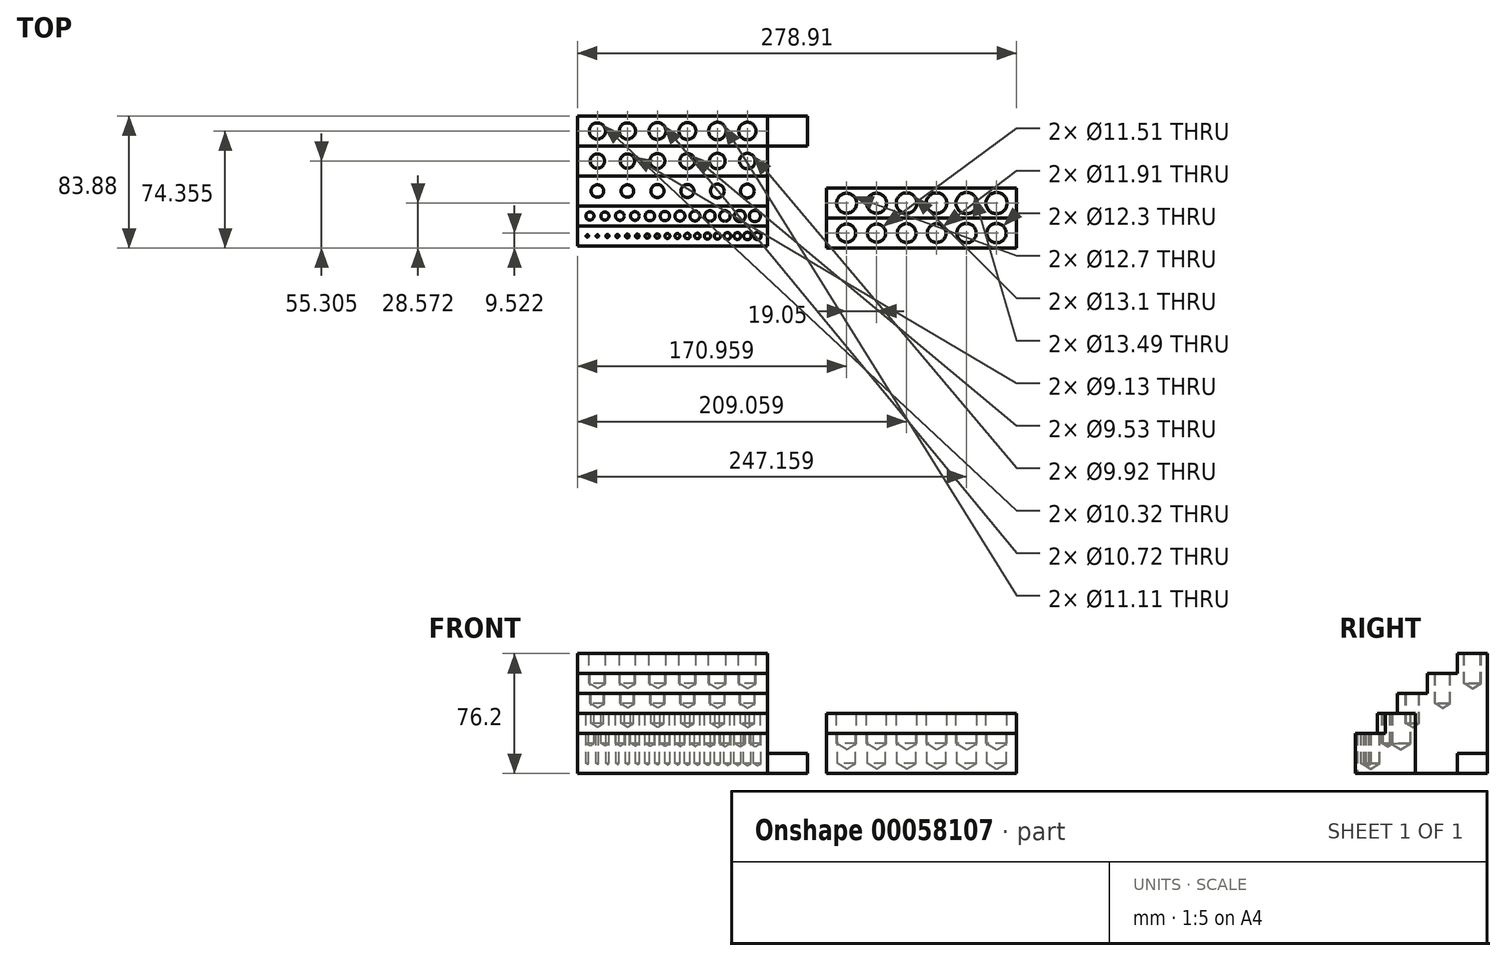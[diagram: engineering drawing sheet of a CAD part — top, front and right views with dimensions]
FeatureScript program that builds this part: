
annotation { "Feature Type Name" : "Feature", "Feature Type Description" : "" }
export const myFeature = defineFeature(function(context is Context, id is Id, definition is map)
    precondition{}
    {
        {
            var Q0;
            Q0=qCreatedBy(makeId("Top.planeOp"),FACE);
            var sketch = newSketch(context, id + "F0", { "sketchPlane" : qUnion([Q0])});
            skLineSegment(sketch, "E0.rect.bottom", {"start": v(60.32, -31.75) * mm, "end": v(-60.33, -31.75) * mm});
            skLineSegment(sketch, "E0.rect.top", {"start": v(60.33, 31.75) * mm, "end": v(-60.32, 31.75) * mm});
            skLineSegment(sketch, "E0.rect.left", {"start": v(60.32, -31.75) * mm, "end": v(60.33, 31.75) * mm});
            skLineSegment(sketch, "E0.rect.right", {"start": v(-60.33, -31.75) * mm, "end": v(-60.32, 31.75) * mm});
            skPoint(sketch, "E0.rect.middle", {"position": v(0, 0) * mm});
            skLineSegment(sketch, "E1", {"start": v(-60.33, 12.7) * mm, "end": v(60.33, 12.7) * mm});
            skLineSegment(sketch, "E2", {"start": v(-60.33, -6.35) * mm, "end": v(60.32, -6.35) * mm});
            skLineSegment(sketch, "E3", {"start": v(-60.33, -19.05) * mm, "end": v(60.33, -19.05) * mm});
            skLineSegment(sketch, "E4", {"start": v(-60.32, 31.75) * mm, "end": v(-60.32, 50.8) * mm});
            skLineSegment(sketch, "E5", {"start": v(-60.33, 50.8) * mm, "end": v(60.32, 50.8) * mm});
            skLineSegment(sketch, "E6", {"start": v(60.33, 31.75) * mm, "end": v(60.33, 50.8) * mm});
            skSolve(sketch);
        }
        {
            var Q0;
            {var subQ0=sQuery(id+"F0.wireOp",EDGE,"E0.rect.top");Q0=makeQuery(id+"F0.imprint","IMPRINT",FACE,{"disambiguationData":[TD([[makeQuery(id+"F0.imprint","IMPRINT",EDGE,{"derivedFrom":subQ0}),1.0]])]});}
            extrude(context, id + "F1", {"entities" : qUnion([Q0]), "depth" : 63.5 * mm});
        }
        {
            var Q0;
            {var subQ0=sQuery(id+"F0.wireOp",EDGE,"E1");Q0=makeQuery(id+"F0.imprint","IMPRINT",FACE,{"disambiguationData":[TD([[makeQuery(id+"F0.imprint","IMPRINT",EDGE,{"derivedFrom":subQ0}),-1.0]])]});}
            extrude(context, id + "F2", {"entities" : qUnion([Q0]), "operationType" : NewBodyOperationType.ADD, "depth" : 50.8 * mm});
        }
        {
            var Q0;
            {var subQ0=sQuery(id+"F0.wireOp",EDGE,"E2");Q0=makeQuery(id+"F0.imprint","IMPRINT",FACE,{"disambiguationData":[TD([[makeQuery(id+"F0.imprint","IMPRINT",EDGE,{"derivedFrom":subQ0}),-1.0]])]});}
            extrude(context, id + "F3", {"entities" : qUnion([Q0]), "operationType" : NewBodyOperationType.ADD, "depth" : 38.1 * mm});
        }
        {
            var Q0;
            {var subQ0=sQuery(id+"F0.wireOp",EDGE,"E0.rect.bottom");Q0=makeQuery(id+"F0.imprint","IMPRINT",FACE,{"disambiguationData":[TD([[makeQuery(id+"F0.imprint","IMPRINT",EDGE,{"derivedFrom":subQ0}),-1.0]])]});}
            extrude(context, id + "F4", {"entities" : qUnion([Q0]), "operationType" : NewBodyOperationType.ADD, "depth" : 25.4 * mm});
        }
        {
            var Q0;
            Q0=makeQuery(id+"F4.opExtrude","CAP_FACE",FACE,{"disambiguationData":[OSD([sQuery(id+"F0.wireOp",EDGE,"E0.rect.bottom"),sQuery(id+"F0.wireOp",EDGE,"E0.rect.left"),sQuery(id+"F0.wireOp",EDGE,"E0.rect.right"),sQuery(id+"F0.wireOp",EDGE,"E3")])],"isStart":false});
            var sketch = newSketch(context, id + "F5", { "sketchPlane" : qUnion([Q0])});
            skPoint(sketch, "E7", {"position": v(-53.97, -25.4) * mm});
            skPoint(sketch, "E8.1.0.0", {"position": v(-47.62, -25.4) * mm});
            skPoint(sketch, "E8.2.0.0", {"position": v(-41.27, -25.4) * mm});
            skPoint(sketch, "E8.3.0.0", {"position": v(-34.92, -25.4) * mm});
            skPoint(sketch, "E8.4.0.0", {"position": v(-28.57, -25.4) * mm});
            skPoint(sketch, "E8.5.0.0", {"position": v(-22.22, -25.4) * mm});
            skPoint(sketch, "E8.6.0.0", {"position": v(-15.87, -25.4) * mm});
            skPoint(sketch, "E8.7.0.0", {"position": v(-9.52, -25.4) * mm});
            skPoint(sketch, "E8.8.0.0", {"position": v(-3.17, -25.4) * mm});
            skPoint(sketch, "E8.9.0.0", {"position": v(3.18, -25.4) * mm});
            skPoint(sketch, "E8.10.0.0", {"position": v(9.53, -25.4) * mm});
            skPoint(sketch, "E8.11.0.0", {"position": v(15.88, -25.4) * mm});
            skPoint(sketch, "E8.12.0.0", {"position": v(22.23, -25.4) * mm});
            skPoint(sketch, "E8.13.0.0", {"position": v(28.58, -25.4) * mm});
            skPoint(sketch, "E8.14.0.0", {"position": v(34.93, -25.4) * mm});
            skPoint(sketch, "E8.15.0.0", {"position": v(41.28, -25.4) * mm});
            skPoint(sketch, "E8.16.0.0", {"position": v(47.63, -25.4) * mm});
            skPoint(sketch, "E8.17.0.0", {"position": v(53.98, -25.4) * mm});
            skLineSegment(sketch, "E8.direction1", {"start": v(-53.97, -25.4) * mm, "end": v(-47.62, -25.4) * mm, "construction": true});
            skSolve(sketch);
        }
        {
            var Q0;
            Q0=sQuery(id+"F5.wireOp",VERTEX,"E7");
            var Q1;
            Q1=sQuery(id+"F5.wireOp",VERTEX,"E8.1.0.0");
            var Q2;
            Q2=makeQuery(id+"F1.opExtrude","SWEPT_BODY",BODY,{"disambiguationData":[OSD([sQuery(id+"F0.wireOp",EDGE,"E0.rect.top"),sQuery(id+"F0.wireOp",EDGE,"E0.rect.left"),sQuery(id+"F0.wireOp",EDGE,"E0.rect.right"),sQuery(id+"F0.wireOp",EDGE,"lhXQ74A1-xkz0-zKio-Q11E-yxSvWY71u6oR")])]});
            hole(context, id + "F6", {"style" : HoleStyle.SIMPLE, "holeDiameter" : 1.59 * mm, "endStyle" : HoleEndStyle.BLIND, "holeDepth" : 19.05 * mm, "locations" : qUnion([Q0, Q1]), "scope" : qUnion([Q2])});
        }
        {
            var Q0;
            Q0=sQuery(id+"F5.wireOp",VERTEX,"E8.2.0.0");
            var Q1;
            Q1=sQuery(id+"F5.wireOp",VERTEX,"E8.3.0.0");
            var Q2;
            Q2=makeQuery(id+"F1.opExtrude","SWEPT_BODY",BODY,{"disambiguationData":[OSD([sQuery(id+"F0.wireOp",EDGE,"E0.rect.top"),sQuery(id+"F0.wireOp",EDGE,"E0.rect.left"),sQuery(id+"F0.wireOp",EDGE,"E0.rect.right"),sQuery(id+"F0.wireOp",EDGE,"lhXQ74A1-xkz0-zKio-Q11E-yxSvWY71u6oR")])]});
            hole(context, id + "F7", {"style" : HoleStyle.SIMPLE, "holeDiameter" : 1.98 * mm, "endStyle" : HoleEndStyle.BLIND, "holeDepth" : 19.05 * mm, "locations" : qUnion([Q0, Q1]), "scope" : qUnion([Q2])});
        }
        {
            var Q0;
            Q0=sQuery(id+"F5.wireOp",VERTEX,"E8.4.0.0");
            var Q1;
            Q1=sQuery(id+"F5.wireOp",VERTEX,"E8.5.0.0");
            var Q2;
            Q2=makeQuery(id+"F1.opExtrude","SWEPT_BODY",BODY,{"disambiguationData":[OSD([sQuery(id+"F0.wireOp",EDGE,"E0.rect.top"),sQuery(id+"F0.wireOp",EDGE,"E0.rect.left"),sQuery(id+"F0.wireOp",EDGE,"E0.rect.right"),sQuery(id+"F0.wireOp",EDGE,"lhXQ74A1-xkz0-zKio-Q11E-yxSvWY71u6oR")])]});
            hole(context, id + "F8", {"style" : HoleStyle.SIMPLE, "holeDiameter" : 2.38 * mm, "endStyle" : HoleEndStyle.BLIND, "holeDepth" : 19.05 * mm, "locations" : qUnion([Q0, Q1]), "scope" : qUnion([Q2])});
        }
        {
            var Q0;
            Q0=sQuery(id+"F5.wireOp",VERTEX,"E8.7.0.0");
            var Q1;
            Q1=sQuery(id+"F5.wireOp",VERTEX,"E8.6.0.0");
            var Q2;
            Q2=makeQuery(id+"F1.opExtrude","SWEPT_BODY",BODY,{"disambiguationData":[OSD([sQuery(id+"F0.wireOp",EDGE,"E0.rect.top"),sQuery(id+"F0.wireOp",EDGE,"E0.rect.left"),sQuery(id+"F0.wireOp",EDGE,"E0.rect.right"),sQuery(id+"F0.wireOp",EDGE,"lhXQ74A1-xkz0-zKio-Q11E-yxSvWY71u6oR")])]});
            hole(context, id + "F9", {"style" : HoleStyle.SIMPLE, "holeDiameter" : 2.78 * mm, "endStyle" : HoleEndStyle.BLIND, "holeDepth" : 19.05 * mm, "locations" : qUnion([Q0, Q1]), "scope" : qUnion([Q2])});
        }
        {
            var Q0;
            Q0=sQuery(id+"F5.wireOp",VERTEX,"E8.8.0.0");
            var Q1;
            Q1=sQuery(id+"F5.wireOp",VERTEX,"E8.9.0.0");
            var Q2;
            Q2=makeQuery(id+"F1.opExtrude","SWEPT_BODY",BODY,{"disambiguationData":[OSD([sQuery(id+"F0.wireOp",EDGE,"E0.rect.top"),sQuery(id+"F0.wireOp",EDGE,"E0.rect.left"),sQuery(id+"F0.wireOp",EDGE,"E0.rect.right"),sQuery(id+"F0.wireOp",EDGE,"lhXQ74A1-xkz0-zKio-Q11E-yxSvWY71u6oR")])]});
            hole(context, id + "F10", {"style" : HoleStyle.SIMPLE, "holeDiameter" : 3.17 * mm, "endStyle" : HoleEndStyle.BLIND, "holeDepth" : 19.05 * mm, "locations" : qUnion([Q0, Q1]), "scope" : qUnion([Q2])});
        }
        {
            var Q0;
            Q0=sQuery(id+"F5.wireOp",VERTEX,"E8.10.0.0");
            var Q1;
            Q1=sQuery(id+"F5.wireOp",VERTEX,"E8.11.0.0");
            var Q2;
            Q2=makeQuery(id+"F1.opExtrude","SWEPT_BODY",BODY,{"disambiguationData":[OSD([sQuery(id+"F0.wireOp",EDGE,"E0.rect.top"),sQuery(id+"F0.wireOp",EDGE,"E0.rect.left"),sQuery(id+"F0.wireOp",EDGE,"E0.rect.right"),sQuery(id+"F0.wireOp",EDGE,"lhXQ74A1-xkz0-zKio-Q11E-yxSvWY71u6oR")])]});
            hole(context, id + "F11", {"style" : HoleStyle.SIMPLE, "holeDiameter" : 3.57 * mm, "endStyle" : HoleEndStyle.BLIND, "holeDepth" : 19.05 * mm, "locations" : qUnion([Q0, Q1]), "scope" : qUnion([Q2])});
        }
        {
            var Q0;
            Q0=sQuery(id+"F5.wireOp",VERTEX,"E8.12.0.0");
            var Q1;
            Q1=sQuery(id+"F5.wireOp",VERTEX,"E8.13.0.0");
            var Q2;
            Q2=makeQuery(id+"F1.opExtrude","SWEPT_BODY",BODY,{"disambiguationData":[OSD([sQuery(id+"F0.wireOp",EDGE,"E0.rect.top"),sQuery(id+"F0.wireOp",EDGE,"E0.rect.left"),sQuery(id+"F0.wireOp",EDGE,"E0.rect.right"),sQuery(id+"F0.wireOp",EDGE,"lhXQ74A1-xkz0-zKio-Q11E-yxSvWY71u6oR")])]});
            hole(context, id + "F12", {"style" : HoleStyle.SIMPLE, "holeDiameter" : 3.97 * mm, "endStyle" : HoleEndStyle.BLIND, "holeDepth" : 19.05 * mm, "locations" : qUnion([Q0, Q1]), "scope" : qUnion([Q2])});
        }
        {
            var Q0;
            Q0=sQuery(id+"F5.wireOp",VERTEX,"E8.14.0.0");
            var Q1;
            Q1=sQuery(id+"F5.wireOp",VERTEX,"E8.15.0.0");
            var Q2;
            Q2=makeQuery(id+"F1.opExtrude","SWEPT_BODY",BODY,{"disambiguationData":[OSD([sQuery(id+"F0.wireOp",EDGE,"E0.rect.top"),sQuery(id+"F0.wireOp",EDGE,"E0.rect.left"),sQuery(id+"F0.wireOp",EDGE,"E0.rect.right"),sQuery(id+"F0.wireOp",EDGE,"lhXQ74A1-xkz0-zKio-Q11E-yxSvWY71u6oR")])]});
            hole(context, id + "F13", {"style" : HoleStyle.SIMPLE, "holeDiameter" : 4.37 * mm, "endStyle" : HoleEndStyle.BLIND, "holeDepth" : 19.05 * mm, "locations" : qUnion([Q0, Q1]), "scope" : qUnion([Q2])});
        }
        {
            var Q0;
            Q0=sQuery(id+"F5.wireOp",VERTEX,"E8.16.0.0");
            var Q1;
            Q1=sQuery(id+"F5.wireOp",VERTEX,"E8.17.0.0");
            var Q2;
            Q2=makeQuery(id+"F1.opExtrude","SWEPT_BODY",BODY,{"disambiguationData":[OSD([sQuery(id+"F0.wireOp",EDGE,"E0.rect.top"),sQuery(id+"F0.wireOp",EDGE,"E0.rect.left"),sQuery(id+"F0.wireOp",EDGE,"E0.rect.right"),sQuery(id+"F0.wireOp",EDGE,"lhXQ74A1-xkz0-zKio-Q11E-yxSvWY71u6oR")])]});
            hole(context, id + "F14", {"style" : HoleStyle.SIMPLE, "holeDiameter" : 4.76 * mm, "endStyle" : HoleEndStyle.BLIND, "holeDepth" : 19.05 * mm, "locations" : qUnion([Q0, Q1]), "scope" : qUnion([Q2])});
        }
        {
            var Q0;
            Q0=makeQuery(id+"F3.opExtrude","CAP_FACE",FACE,{"disambiguationData":[OSD([sQuery(id+"F0.wireOp",EDGE,"E0.rect.left"),sQuery(id+"F0.wireOp",EDGE,"E0.rect.right"),sQuery(id+"F0.wireOp",EDGE,"E2"),sQuery(id+"F0.wireOp",EDGE,"E3")])],"isStart":false});
            var sketch = newSketch(context, id + "F15", { "sketchPlane" : qUnion([Q0])});
            skPoint(sketch, "E9", {"position": v(-52.39, -12.7) * mm});
            skPoint(sketch, "E10.1.0.0", {"position": v(-42.86, -12.7) * mm});
            skPoint(sketch, "E10.2.0.0", {"position": v(-33.34, -12.7) * mm});
            skPoint(sketch, "E10.3.0.0", {"position": v(-23.81, -12.7) * mm});
            skPoint(sketch, "E10.4.0.0", {"position": v(-14.29, -12.7) * mm});
            skPoint(sketch, "E10.5.0.0", {"position": v(-4.76, -12.7) * mm});
            skPoint(sketch, "E10.6.0.0", {"position": v(4.76, -12.7) * mm});
            skPoint(sketch, "E10.7.0.0", {"position": v(14.29, -12.7) * mm});
            skPoint(sketch, "E10.8.0.0", {"position": v(23.81, -12.7) * mm});
            skLineSegment(sketch, "E10.direction1", {"start": v(-52.39, -12.7) * mm, "end": v(-42.86, -12.7) * mm, "construction": true});
            skPoint(sketch, "E11.0.9.0", {"position": v(33.34, -12.7) * mm});
            skPoint(sketch, "E11.0.10.0", {"position": v(42.86, -12.7) * mm});
            skPoint(sketch, "E12.0.11.0", {"position": v(52.39, -12.7) * mm});
            skSolve(sketch);
        }
        {
            var Q0;
            Q0=sQuery(id+"F15.wireOp",VERTEX,"E9");
            var Q1;
            Q1=sQuery(id+"F15.wireOp",VERTEX,"E10.direction1.end");
            var Q2;
            Q2=makeQuery(id+"F1.opExtrude","SWEPT_BODY",BODY,{"disambiguationData":[OSD([sQuery(id+"F0.wireOp",EDGE,"E0.rect.top"),sQuery(id+"F0.wireOp",EDGE,"E0.rect.left"),sQuery(id+"F0.wireOp",EDGE,"E0.rect.right"),sQuery(id+"F0.wireOp",EDGE,"lhXQ74A1-xkz0-zKio-Q11E-yxSvWY71u6oR")])]});
            hole(context, id + "F16", {"style" : HoleStyle.SIMPLE, "holeDiameter" : 5.16 * mm, "endStyle" : HoleEndStyle.BLIND, "holeDepth" : 19.05 * mm, "locations" : qUnion([Q0, Q1]), "scope" : qUnion([Q2])});
        }
        {
            var Q0;
            Q0=sQuery(id+"F15.wireOp",VERTEX,"E10.2.0.0");
            var Q1;
            Q1=sQuery(id+"F15.wireOp",VERTEX,"E10.3.0.0");
            var Q2;
            Q2=makeQuery(id+"F1.opExtrude","SWEPT_BODY",BODY,{"disambiguationData":[OSD([sQuery(id+"F0.wireOp",EDGE,"E0.rect.top"),sQuery(id+"F0.wireOp",EDGE,"E0.rect.left"),sQuery(id+"F0.wireOp",EDGE,"E0.rect.right"),sQuery(id+"F0.wireOp",EDGE,"lhXQ74A1-xkz0-zKio-Q11E-yxSvWY71u6oR")])]});
            hole(context, id + "F17", {"style" : HoleStyle.SIMPLE, "holeDiameter" : 5.56 * mm, "endStyle" : HoleEndStyle.BLIND, "holeDepth" : 19.05 * mm, "locations" : qUnion([Q0, Q1]), "scope" : qUnion([Q2])});
        }
        {
            var Q0;
            Q0=sQuery(id+"F15.wireOp",VERTEX,"E10.4.0.0");
            var Q1;
            Q1=sQuery(id+"F15.wireOp",VERTEX,"E10.5.0.0");
            var Q2;
            Q2=makeQuery(id+"F1.opExtrude","SWEPT_BODY",BODY,{"disambiguationData":[OSD([sQuery(id+"F0.wireOp",EDGE,"E0.rect.top"),sQuery(id+"F0.wireOp",EDGE,"E0.rect.left"),sQuery(id+"F0.wireOp",EDGE,"E0.rect.right"),sQuery(id+"F0.wireOp",EDGE,"lhXQ74A1-xkz0-zKio-Q11E-yxSvWY71u6oR")])]});
            hole(context, id + "F18", {"style" : HoleStyle.SIMPLE, "holeDiameter" : 5.95 * mm, "endStyle" : HoleEndStyle.BLIND, "holeDepth" : 19.05 * mm, "locations" : qUnion([Q0, Q1]), "scope" : qUnion([Q2])});
        }
        {
            var Q0;
            Q0=sQuery(id+"F15.wireOp",VERTEX,"E10.6.0.0");
            var Q1;
            Q1=sQuery(id+"F15.wireOp",VERTEX,"E10.7.0.0");
            var Q2;
            Q2=makeQuery(id+"F1.opExtrude","SWEPT_BODY",BODY,{"disambiguationData":[OSD([sQuery(id+"F0.wireOp",EDGE,"E0.rect.top"),sQuery(id+"F0.wireOp",EDGE,"E0.rect.left"),sQuery(id+"F0.wireOp",EDGE,"E0.rect.right"),sQuery(id+"F0.wireOp",EDGE,"lhXQ74A1-xkz0-zKio-Q11E-yxSvWY71u6oR")])]});
            hole(context, id + "F19", {"style" : HoleStyle.SIMPLE, "holeDiameter" : 6.35 * mm, "endStyle" : HoleEndStyle.BLIND, "holeDepth" : 19.05 * mm, "locations" : qUnion([Q0, Q1]), "scope" : qUnion([Q2])});
        }
        {
            var Q0;
            Q0=sQuery(id+"F15.wireOp",VERTEX,"E10.8.0.0");
            var Q1;
            Q1=sQuery(id+"F15.wireOp",VERTEX,"E11.0.9.0");
            var Q2;
            Q2=makeQuery(id+"F1.opExtrude","SWEPT_BODY",BODY,{"disambiguationData":[OSD([sQuery(id+"F0.wireOp",EDGE,"E0.rect.top"),sQuery(id+"F0.wireOp",EDGE,"E0.rect.left"),sQuery(id+"F0.wireOp",EDGE,"E0.rect.right"),sQuery(id+"F0.wireOp",EDGE,"lhXQ74A1-xkz0-zKio-Q11E-yxSvWY71u6oR")])]});
            hole(context, id + "F20", {"style" : HoleStyle.SIMPLE, "holeDiameter" : 6.75 * mm, "endStyle" : HoleEndStyle.BLIND, "holeDepth" : 19.05 * mm, "locations" : qUnion([Q0, Q1]), "scope" : qUnion([Q2])});
        }
        {
            var Q0;
            Q0=sQuery(id+"F15.wireOp",VERTEX,"E11.0.10.0");
            var Q1;
            Q1=sQuery(id+"F15.wireOp",VERTEX,"E12.0.11.0");
            var Q2;
            Q2=makeQuery(id+"F1.opExtrude","SWEPT_BODY",BODY,{"disambiguationData":[OSD([sQuery(id+"F0.wireOp",EDGE,"E0.rect.top"),sQuery(id+"F0.wireOp",EDGE,"E0.rect.left"),sQuery(id+"F0.wireOp",EDGE,"E0.rect.right"),sQuery(id+"F0.wireOp",EDGE,"lhXQ74A1-xkz0-zKio-Q11E-yxSvWY71u6oR")])]});
            hole(context, id + "F21", {"style" : HoleStyle.SIMPLE, "holeDiameter" : 7.14 * mm, "endStyle" : HoleEndStyle.BLIND, "holeDepth" : 19.05 * mm, "locations" : qUnion([Q0, Q1]), "scope" : qUnion([Q2])});
        }
        {
            var Q0;
            Q0=makeQuery(id+"F2.opExtrude","CAP_FACE",FACE,{"disambiguationData":[OSD([sQuery(id+"F0.wireOp",EDGE,"E0.rect.left"),sQuery(id+"F0.wireOp",EDGE,"E0.rect.right"),sQuery(id+"F0.wireOp",EDGE,"E1"),sQuery(id+"F0.wireOp",EDGE,"E2")])],"isStart":false});
            var sketch = newSketch(context, id + "F22", { "sketchPlane" : qUnion([Q0])});
            skPoint(sketch, "E13", {"position": v(-47.63, 3.17) * mm});
            skPoint(sketch, "E14.1.0.0", {"position": v(-28.58, 3.17) * mm});
            skPoint(sketch, "E14.2.0.0", {"position": v(-9.53, 3.17) * mm});
            skPoint(sketch, "E14.3.0.0", {"position": v(9.52, 3.17) * mm});
            skPoint(sketch, "E14.4.0.0", {"position": v(28.57, 3.17) * mm});
            skLineSegment(sketch, "E14.direction1", {"start": v(-47.63, 3.17) * mm, "end": v(-28.58, 3.17) * mm, "construction": true});
            skPoint(sketch, "E15.0.5.0", {"position": v(47.62, 3.18) * mm});
            skSolve(sketch);
        }
        {
            var Q0;
            Q0=sQuery(id+"F22.wireOp",VERTEX,"E13");
            var Q1;
            Q1=sQuery(id+"F22.wireOp",VERTEX,"E14.1.0.0");
            var Q2;
            Q2=makeQuery(id+"F1.opExtrude","SWEPT_BODY",BODY,{"disambiguationData":[OSD([sQuery(id+"F0.wireOp",EDGE,"E0.rect.top"),sQuery(id+"F0.wireOp",EDGE,"E0.rect.left"),sQuery(id+"F0.wireOp",EDGE,"E0.rect.right"),sQuery(id+"F0.wireOp",EDGE,"E1")])]});
            hole(context, id + "F23", {"style" : HoleStyle.SIMPLE, "holeDiameter" : 7.94 * mm, "endStyle" : HoleEndStyle.BLIND, "holeDepth" : 19.05 * mm, "locations" : qUnion([Q0, Q1]), "scope" : qUnion([Q2])});
        }
        {
            var Q0;
            Q0=sQuery(id+"F22.wireOp",VERTEX,"E14.2.0.0");
            var Q1;
            Q1=sQuery(id+"F22.wireOp",VERTEX,"E14.3.0.0");
            var Q2;
            Q2=makeQuery(id+"F1.opExtrude","SWEPT_BODY",BODY,{"disambiguationData":[OSD([sQuery(id+"F0.wireOp",EDGE,"E0.rect.top"),sQuery(id+"F0.wireOp",EDGE,"E0.rect.left"),sQuery(id+"F0.wireOp",EDGE,"E0.rect.right"),sQuery(id+"F0.wireOp",EDGE,"E1")])]});
            hole(context, id + "F24", {"style" : HoleStyle.SIMPLE, "holeDiameter" : 8.33 * mm, "endStyle" : HoleEndStyle.BLIND, "holeDepth" : 19.05 * mm, "locations" : qUnion([Q0, Q1]), "scope" : qUnion([Q2])});
        }
        {
            var Q0;
            Q0=sQuery(id+"F22.wireOp",VERTEX,"E14.4.0.0");
            var Q1;
            Q1=sQuery(id+"F22.wireOp",VERTEX,"E15.0.5.0");
            var Q2;
            Q2=makeQuery(id+"F1.opExtrude","SWEPT_BODY",BODY,{"disambiguationData":[OSD([sQuery(id+"F0.wireOp",EDGE,"E0.rect.top"),sQuery(id+"F0.wireOp",EDGE,"E0.rect.left"),sQuery(id+"F0.wireOp",EDGE,"E0.rect.right"),sQuery(id+"F0.wireOp",EDGE,"E1")])]});
            hole(context, id + "F25", {"style" : HoleStyle.SIMPLE, "holeDiameter" : 8.73 * mm, "endStyle" : HoleEndStyle.BLIND, "holeDepth" : 19.05 * mm, "locations" : qUnion([Q0, Q1]), "scope" : qUnion([Q2])});
        }
        {
            var Q0;
            Q0=makeQuery(id+"F1.opExtrude","CAP_FACE",FACE,{"disambiguationData":[OSD([sQuery(id+"F0.wireOp",EDGE,"E0.rect.top"),sQuery(id+"F0.wireOp",EDGE,"E0.rect.left"),sQuery(id+"F0.wireOp",EDGE,"E0.rect.right"),sQuery(id+"F0.wireOp",EDGE,"E1")])],"isStart":false});
            var sketch = newSketch(context, id + "F26", { "sketchPlane" : qUnion([Q0])});
            skPoint(sketch, "E16", {"position": v(-47.62, 22.23) * mm});
            skPoint(sketch, "E17.1.0.0", {"position": v(-28.57, 22.23) * mm});
            skPoint(sketch, "E17.2.0.0", {"position": v(-9.52, 22.23) * mm});
            skPoint(sketch, "E17.3.0.0", {"position": v(9.53, 22.23) * mm});
            skPoint(sketch, "E17.4.0.0", {"position": v(28.58, 22.23) * mm});
            skPoint(sketch, "E17.5.0.0", {"position": v(47.62, 22.23) * mm});
            skLineSegment(sketch, "E17.direction1", {"start": v(-47.62, 22.23) * mm, "end": v(-28.57, 22.23) * mm, "construction": true});
            skSolve(sketch);
        }
        {
            var Q0;
            Q0=sQuery(id+"F26.wireOp",VERTEX,"E16");
            var Q1;
            Q1=sQuery(id+"F26.wireOp",VERTEX,"E17.1.0.0");
            var Q2;
            Q2=makeQuery(id+"F1.opExtrude","SWEPT_BODY",BODY,{"disambiguationData":[OSD([sQuery(id+"F0.wireOp",EDGE,"E0.rect.top"),sQuery(id+"F0.wireOp",EDGE,"E0.rect.left"),sQuery(id+"F0.wireOp",EDGE,"E0.rect.right"),sQuery(id+"F0.wireOp",EDGE,"E1")])]});
            hole(context, id + "F27", {"style" : HoleStyle.SIMPLE, "holeDiameter" : 9.13 * mm, "endStyle" : HoleEndStyle.BLIND, "holeDepth" : 19.05 * mm, "locations" : qUnion([Q0, Q1]), "scope" : qUnion([Q2])});
        }
        {
            var Q0;
            Q0=sQuery(id+"F26.wireOp",VERTEX,"E17.2.0.0");
            var Q1;
            Q1=sQuery(id+"F26.wireOp",VERTEX,"E17.3.0.0");
            var Q2;
            Q2=makeQuery(id+"F1.opExtrude","SWEPT_BODY",BODY,{"disambiguationData":[OSD([sQuery(id+"F0.wireOp",EDGE,"E0.rect.top"),sQuery(id+"F0.wireOp",EDGE,"E0.rect.left"),sQuery(id+"F0.wireOp",EDGE,"E0.rect.right"),sQuery(id+"F0.wireOp",EDGE,"E1")])]});
            hole(context, id + "F28", {"style" : HoleStyle.SIMPLE, "holeDiameter" : 9.52 * mm, "endStyle" : HoleEndStyle.BLIND, "holeDepth" : 19.05 * mm, "locations" : qUnion([Q0, Q1]), "scope" : qUnion([Q2])});
        }
        {
            var Q0;
            Q0=sQuery(id+"F26.wireOp",VERTEX,"E17.4.0.0");
            var Q1;
            Q1=sQuery(id+"F26.wireOp",VERTEX,"E17.5.0.0");
            var Q2;
            Q2=makeQuery(id+"F1.opExtrude","SWEPT_BODY",BODY,{"disambiguationData":[OSD([sQuery(id+"F0.wireOp",EDGE,"E0.rect.top"),sQuery(id+"F0.wireOp",EDGE,"E0.rect.left"),sQuery(id+"F0.wireOp",EDGE,"E0.rect.right"),sQuery(id+"F0.wireOp",EDGE,"E1")])]});
            hole(context, id + "F29", {"style" : HoleStyle.SIMPLE, "holeDiameter" : 9.92 * mm, "endStyle" : HoleEndStyle.BLIND, "holeDepth" : 19.05 * mm, "locations" : qUnion([Q0, Q1]), "scope" : qUnion([Q2])});
        }
        {
            var Q0;
            Q0=makeQuery(id+"F0.imprint","IMPRINT",FACE,{"disambiguationData":[TD([[makeQuery(id+"F0.imprint","IMPRINT",EDGE,{"derivedFrom":sQuery(id+"F0.wireOp",EDGE,"E0.rect.top")}),-1.0]])]});
            extrude(context, id + "F30", {"entities" : qUnion([Q0]), "operationType" : NewBodyOperationType.ADD, "depth" : 76.2 * mm});
        }
        {
            var Q0;
            Q0=makeQuery(id+"F30.opExtrude","CAP_FACE",FACE,{"disambiguationData":[OSD([sQuery(id+"F0.wireOp",EDGE,"E0.rect.top"),sQuery(id+"F0.wireOp",EDGE,"E4"),sQuery(id+"F0.wireOp",EDGE,"E5"),sQuery(id+"F0.wireOp",EDGE,"E6")])],"isStart":false});
            var sketch = newSketch(context, id + "F31", { "sketchPlane" : qUnion([Q0])});
            skPoint(sketch, "E18", {"position": v(-47.62, 41.28) * mm});
            skPoint(sketch, "E19.1.0.0", {"position": v(-28.57, 41.28) * mm});
            skPoint(sketch, "E19.2.0.0", {"position": v(-9.52, 41.28) * mm});
            skPoint(sketch, "E19.3.0.0", {"position": v(9.53, 41.28) * mm});
            skPoint(sketch, "E19.4.0.0", {"position": v(28.58, 41.28) * mm});
            skPoint(sketch, "E19.5.0.0", {"position": v(47.63, 41.28) * mm});
            skLineSegment(sketch, "E19.direction1", {"start": v(-47.62, 41.28) * mm, "end": v(-28.57, 41.28) * mm, "construction": true});
            skSolve(sketch);
        }
        {
            var Q0;
            Q0=sQuery(id+"F31.wireOp",VERTEX,"E18");
            var Q1;
            Q1=sQuery(id+"F31.wireOp",VERTEX,"E19.1.0.0");
            var Q2;
            Q2=makeQuery(id+"F1.opExtrude","SWEPT_BODY",BODY,{"disambiguationData":[OSD([sQuery(id+"F0.wireOp",EDGE,"E0.rect.top"),sQuery(id+"F0.wireOp",EDGE,"E0.rect.left"),sQuery(id+"F0.wireOp",EDGE,"E0.rect.right"),sQuery(id+"F0.wireOp",EDGE,"E1")])]});
            hole(context, id + "F32", {"style" : HoleStyle.SIMPLE, "holeDiameter" : 10.32 * mm, "endStyle" : HoleEndStyle.BLIND, "holeDepth" : 19.05 * mm, "locations" : qUnion([Q0, Q1]), "scope" : qUnion([Q2])});
        }
        {
            var Q0;
            Q0=sQuery(id+"F31.wireOp",VERTEX,"E19.2.0.0");
            var Q1;
            Q1=sQuery(id+"F31.wireOp",VERTEX,"E19.3.0.0");
            var Q2;
            Q2=makeQuery(id+"F1.opExtrude","SWEPT_BODY",BODY,{"disambiguationData":[OSD([sQuery(id+"F0.wireOp",EDGE,"E0.rect.top"),sQuery(id+"F0.wireOp",EDGE,"E0.rect.left"),sQuery(id+"F0.wireOp",EDGE,"E0.rect.right"),sQuery(id+"F0.wireOp",EDGE,"E1")])]});
            hole(context, id + "F33", {"style" : HoleStyle.SIMPLE, "holeDiameter" : 10.72 * mm, "endStyle" : HoleEndStyle.BLIND, "holeDepth" : 19.05 * mm, "locations" : qUnion([Q0, Q1]), "scope" : qUnion([Q2])});
        }
        {
            var Q0;
            Q0=sQuery(id+"F31.wireOp",VERTEX,"E19.4.0.0");
            var Q1;
            Q1=sQuery(id+"F31.wireOp",VERTEX,"E19.5.0.0");
            var Q2;
            Q2=makeQuery(id+"F1.opExtrude","SWEPT_BODY",BODY,{"disambiguationData":[OSD([sQuery(id+"F0.wireOp",EDGE,"E0.rect.top"),sQuery(id+"F0.wireOp",EDGE,"E0.rect.left"),sQuery(id+"F0.wireOp",EDGE,"E0.rect.right"),sQuery(id+"F0.wireOp",EDGE,"E1")])]});
            hole(context, id + "F34", {"style" : HoleStyle.SIMPLE, "holeDiameter" : 11.1 * mm, "endStyle" : HoleEndStyle.BLIND, "holeDepth" : 19.05 * mm, "locations" : qUnion([Q0, Q1]), "scope" : qUnion([Q2])});
        }
        {
            var Q0;
            {var subQ0=sQuery(id+"F0.wireOp",EDGE,"E0.rect.left");Q0=makeQuery(id+"F30.boolean.opBoolean","MERGE",FACE,{"derivedFrom":[makeQuery(id+"F4.boolean.opBoolean","MERGE",FACE,{"derivedFrom":[makeQuery(id+"F3.boolean.opBoolean","MERGE",FACE,{"derivedFrom":[makeQuery(id+"F2.boolean.opBoolean","MERGE",FACE,{"derivedFrom":[makeQuery(id+"F1.opExtrude","SWEPT_FACE",FACE,{"disambiguationData":[OSD([subQ0])]}),makeQuery(id+"F2.opExtrude","SWEPT_FACE",FACE,{"disambiguationData":[OSD([subQ0])]})]}),makeQuery(id+"F3.opExtrude","SWEPT_FACE",FACE,{"disambiguationData":[OSD([subQ0])]})]}),makeQuery(id+"F4.opExtrude","SWEPT_FACE",FACE,{"disambiguationData":[OSD([subQ0])]})]}),makeQuery(id+"F30.opExtrude","SWEPT_FACE",FACE,{"disambiguationData":[OSD([sQuery(id+"F0.wireOp",EDGE,"E6")])]})]});}
            var sketch = newSketch(context, id + "F35", { "sketchPlane" : qUnion([Q0])});
            skLineSegment(sketch, "E20.bottom", {"start": v(50.8, 0) * mm, "end": v(31.75, 0) * mm});
            skLineSegment(sketch, "E20.top", {"start": v(50.8, 12.7) * mm, "end": v(31.75, 12.7) * mm});
            skLineSegment(sketch, "E20.left", {"start": v(50.8, 0) * mm, "end": v(50.8, 12.7) * mm});
            skLineSegment(sketch, "E20.right", {"start": v(31.75, 0) * mm, "end": v(31.75, 12.7) * mm});
            skSolve(sketch);
        }
        {
            var Q0;
            Q0 = qSketchRegion(id + "F35", true);
            extrude(context, id + "F36", {"entities" : qUnion([Q0]), "operationType" : NewBodyOperationType.ADD, "depth" : 25.4 * mm});
        }
        {
            var Q0;
            Q0=qCreatedBy(makeId("Top.planeOp"),FACE);
            var sketch = newSketch(context, id + "F37", { "sketchPlane" : qUnion([Q0])});
            skLineSegment(sketch, "E21.rect.bottom", {"start": v(218.59, -33.08) * mm, "end": v(97.94, -33.08) * mm});
            skLineSegment(sketch, "E21.rect.top", {"start": v(218.59, 49.47) * mm, "end": v(97.94, 49.47) * mm});
            skLineSegment(sketch, "E21.rect.left", {"start": v(218.59, -33.08) * mm, "end": v(218.59, 49.47) * mm});
            skLineSegment(sketch, "E21.rect.right", {"start": v(97.94, -33.08) * mm, "end": v(97.94, 49.47) * mm});
            skPoint(sketch, "E21.rect.middle", {"position": v(158.26, 8.2) * mm});
            skLineSegment(sketch, "E22", {"start": v(97.94, -14.03) * mm, "end": v(218.59, -14.03) * mm});
            skLineSegment(sketch, "E23", {"start": v(97.94, 5.02) * mm, "end": v(218.59, 5.02) * mm});
            skSolve(sketch);
        }
        {
            var Q0;
            {var subQ0=sQuery(id+"F37.wireOp",EDGE,"E21.rect.bottom");Q0=makeQuery(id+"F37.imprint","IMPRINT",FACE,{"disambiguationData":[TD([[makeQuery(id+"F37.imprint","IMPRINT",EDGE,{"derivedFrom":subQ0}),-1.0]])]});}
            extrude(context, id + "F38", {"entities" : qUnion([Q0]), "depth" : 25.4 * mm});
        }
        {
            var Q0;
            Q0=makeQuery(id+"F38.opExtrude","CAP_FACE",FACE,{"disambiguationData":[OSD([sQuery(id+"F37.wireOp",EDGE,"E21.rect.bottom"),sQuery(id+"F37.wireOp",EDGE,"E21.rect.left"),sQuery(id+"F37.wireOp",EDGE,"E21.rect.right"),sQuery(id+"F37.wireOp",EDGE,"E22")])],"isStart":false});
            var sketch = newSketch(context, id + "F39", { "sketchPlane" : qUnion([Q0])});
            skPoint(sketch, "E24", {"position": v(110.64, -23.56) * mm});
            skPoint(sketch, "E25.1.0.0", {"position": v(129.69, -23.56) * mm});
            skPoint(sketch, "E25.2.0.0", {"position": v(148.74, -23.56) * mm});
            skPoint(sketch, "E25.3.0.0", {"position": v(167.79, -23.56) * mm});
            skPoint(sketch, "E25.4.0.0", {"position": v(186.84, -23.56) * mm});
            skPoint(sketch, "E25.5.0.0", {"position": v(205.89, -23.56) * mm});
            skLineSegment(sketch, "E25.direction1", {"start": v(110.64, -23.56) * mm, "end": v(129.69, -23.56) * mm, "construction": true});
            skSolve(sketch);
        }
        {
            var Q0;
            Q0=sQuery(id+"F39.wireOp",VERTEX,"E24");
            var Q1;
            Q1=sQuery(id+"F39.wireOp",VERTEX,"E25.1.0.0");
            var Q2;
            Q2=makeQuery(id+"F38.opExtrude","SWEPT_BODY",BODY,{"disambiguationData":[OSD([sQuery(id+"F37.wireOp",EDGE,"E21.rect.bottom"),sQuery(id+"F37.wireOp",EDGE,"E21.rect.left"),sQuery(id+"F37.wireOp",EDGE,"E21.rect.right"),sQuery(id+"F37.wireOp",EDGE,"E22")])]});
            hole(context, id + "F40", {"style" : HoleStyle.SIMPLE, "holeDiameter" : 11.5 * mm, "endStyle" : HoleEndStyle.BLIND, "holeDepth" : 19.05 * mm, "locations" : qUnion([Q0, Q1]), "scope" : qUnion([Q2])});
        }
        {
            var Q0;
            Q0=sQuery(id+"F39.wireOp",VERTEX,"E25.2.0.0");
            var Q1;
            Q1=sQuery(id+"F39.wireOp",VERTEX,"E25.3.0.0");
            var Q2;
            Q2=makeQuery(id+"F38.opExtrude","SWEPT_BODY",BODY,{"disambiguationData":[OSD([sQuery(id+"F37.wireOp",EDGE,"E21.rect.bottom"),sQuery(id+"F37.wireOp",EDGE,"E21.rect.left"),sQuery(id+"F37.wireOp",EDGE,"E21.rect.right"),sQuery(id+"F37.wireOp",EDGE,"E22")])]});
            hole(context, id + "F41", {"style" : HoleStyle.SIMPLE, "holeDiameter" : 11.9 * mm, "endStyle" : HoleEndStyle.BLIND, "holeDepth" : 19.05 * mm, "locations" : qUnion([Q0, Q1]), "scope" : qUnion([Q2])});
        }
        {
            var Q0;
            Q0=sQuery(id+"F39.wireOp",VERTEX,"E25.4.0.0");
            var Q1;
            Q1=sQuery(id+"F39.wireOp",VERTEX,"E25.5.0.0");
            var Q2;
            Q2=makeQuery(id+"F38.opExtrude","SWEPT_BODY",BODY,{"disambiguationData":[OSD([sQuery(id+"F37.wireOp",EDGE,"E21.rect.bottom"),sQuery(id+"F37.wireOp",EDGE,"E21.rect.left"),sQuery(id+"F37.wireOp",EDGE,"E21.rect.right"),sQuery(id+"F37.wireOp",EDGE,"E22")])]});
            hole(context, id + "F42", {"style" : HoleStyle.SIMPLE, "holeDiameter" : 12.3 * mm, "endStyle" : HoleEndStyle.BLIND, "holeDepth" : 19.05 * mm, "locations" : qUnion([Q0, Q1]), "scope" : qUnion([Q2])});
        }
        {
            var Q0;
            {var subQ0=sQuery(id+"F37.wireOp",EDGE,"E22");Q0=makeQuery(id+"F37.imprint","IMPRINT",FACE,{"disambiguationData":[TD([[makeQuery(id+"F37.imprint","IMPRINT",EDGE,{"derivedFrom":subQ0}),1.0]])]});}
            extrude(context, id + "F43", {"entities" : qUnion([Q0]), "operationType" : NewBodyOperationType.ADD, "depth" : 38.1 * mm});
        }
        {
            var Q0;
            Q0=makeQuery(id+"F43.opExtrude","CAP_FACE",FACE,{"disambiguationData":[OSD([sQuery(id+"F37.wireOp",EDGE,"E21.rect.left"),sQuery(id+"F37.wireOp",EDGE,"E21.rect.right"),sQuery(id+"F37.wireOp",EDGE,"E22"),sQuery(id+"F37.wireOp",EDGE,"E23")])],"isStart":false});
            var sketch = newSketch(context, id + "F44", { "sketchPlane" : qUnion([Q0])});
            skPoint(sketch, "E26", {"position": v(110.64, -4.5) * mm});
            skPoint(sketch, "E27.1.0.0", {"position": v(129.69, -4.5) * mm});
            skPoint(sketch, "E27.2.0.0", {"position": v(148.74, -4.5) * mm});
            skLineSegment(sketch, "E27.direction1", {"start": v(110.64, -4.5) * mm, "end": v(129.69, -4.5) * mm, "construction": true});
            skPoint(sketch, "E28.0.3.0", {"position": v(167.79, -4.5) * mm});
            skPoint(sketch, "E28.0.4.0", {"position": v(186.84, -4.5) * mm});
            skPoint(sketch, "E28.0.5.0", {"position": v(205.89, -4.5) * mm});
            skSolve(sketch);
        }
        {
            var Q0;
            Q0=sQuery(id+"F44.wireOp",VERTEX,"E26");
            var Q1;
            Q1=sQuery(id+"F44.wireOp",VERTEX,"E27.1.0.0");
            var Q2;
            Q2=makeQuery(id+"F38.opExtrude","SWEPT_BODY",BODY,{"disambiguationData":[OSD([sQuery(id+"F37.wireOp",EDGE,"E21.rect.bottom"),sQuery(id+"F37.wireOp",EDGE,"E21.rect.left"),sQuery(id+"F37.wireOp",EDGE,"E21.rect.right"),sQuery(id+"F37.wireOp",EDGE,"E22")])]});
            hole(context, id + "F45", {"style" : HoleStyle.SIMPLE, "holeDiameter" : 12.7 * mm, "endStyle" : HoleEndStyle.BLIND, "holeDepth" : 19.05 * mm, "locations" : qUnion([Q0, Q1]), "scope" : qUnion([Q2])});
        }
        {
            var Q0;
            Q0=sQuery(id+"F44.wireOp",VERTEX,"E28.0.3.0");
            var Q1;
            Q1=sQuery(id+"F44.wireOp",VERTEX,"E27.2.0.0");
            var Q2;
            Q2=makeQuery(id+"F38.opExtrude","SWEPT_BODY",BODY,{"disambiguationData":[OSD([sQuery(id+"F37.wireOp",EDGE,"E21.rect.bottom"),sQuery(id+"F37.wireOp",EDGE,"E21.rect.left"),sQuery(id+"F37.wireOp",EDGE,"E21.rect.right"),sQuery(id+"F37.wireOp",EDGE,"E22")])]});
            hole(context, id + "F46", {"style" : HoleStyle.SIMPLE, "holeDiameter" : 13.1 * mm, "endStyle" : HoleEndStyle.BLIND, "holeDepth" : 19.05 * mm, "locations" : qUnion([Q0, Q1]), "scope" : qUnion([Q2])});
        }
        {
            var Q0;
            Q0=sQuery(id+"F44.wireOp",VERTEX,"E28.0.4.0");
            var Q1;
            Q1=sQuery(id+"F44.wireOp",VERTEX,"E28.0.5.0");
            var Q2;
            Q2=makeQuery(id+"F38.opExtrude","SWEPT_BODY",BODY,{"disambiguationData":[OSD([sQuery(id+"F37.wireOp",EDGE,"E21.rect.bottom"),sQuery(id+"F37.wireOp",EDGE,"E21.rect.left"),sQuery(id+"F37.wireOp",EDGE,"E21.rect.right"),sQuery(id+"F37.wireOp",EDGE,"E22")])]});
            hole(context, id + "F47", {"style" : HoleStyle.SIMPLE, "holeDiameter" : 13.5 * mm, "endStyle" : HoleEndStyle.BLIND, "holeDepth" : 19.05 * mm, "locations" : qUnion([Q0, Q1]), "scope" : qUnion([Q2])});
        }
    });
